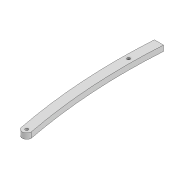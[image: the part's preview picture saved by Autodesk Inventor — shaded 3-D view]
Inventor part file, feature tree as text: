
AUTODESK INVENTOR PART (.ipt)
format: ipt  version: 2022 (Build 260153000, 153)  size: 110,080 bytes
history: native  units: mm
features: extrude x2, sketch x1
ambient origin geometry x8: Origin, YZ Plane, XZ Plane, XY Plane, X Axis, Y Axis, Z Axis, Center Point
bodies: Solid1 (feature_tree)
feature tree (3):
  extrude  "Extrusion1"  Depth=10.0mm
  extrude  "Extrusion2"  Depth=10.0mm
  sketch  "Sketch2"  dims[d0=3.3mm d1=3.3mm d2=10.0mm d3=288.984mm d6=6.0mm d7=0.0mm d14=3.3mm d15=231.585mm d18=600.0mm d19=600.0mm d20=3.3mm d21=122.909mm d22=10.0mm d23=0.0mm]
